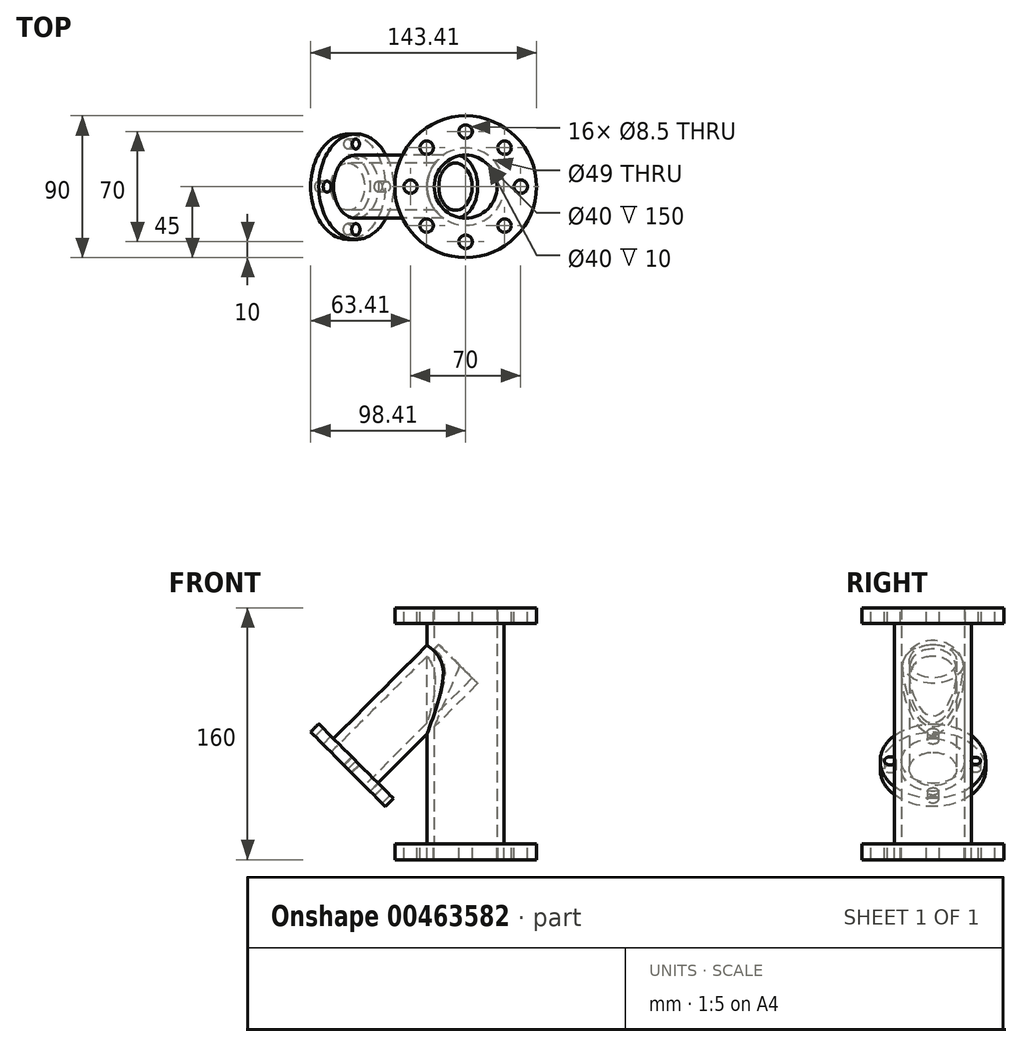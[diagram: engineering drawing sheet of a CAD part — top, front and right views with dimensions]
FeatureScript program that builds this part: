
annotation { "Feature Type Name" : "Feature", "Feature Type Description" : "" }
export const myFeature = defineFeature(function(context is Context, id is Id, definition is map)
    precondition{}
    {
        {
            var Q0;
            Q0=qCreatedBy(makeId("Top.planeOp"),FACE);
            var sketch = newSketch(context, id + "F0", { "sketchPlane" : qUnion([Q0])});
            skCircle(sketch, "E0", {"center": v(0, 0) * mm, "radius": 45 * mm});
            skCircle(sketch, "E1", {"center": v(0, 0) * mm, "radius": 35 * mm, "construction": true});
            skCircle(sketch, "E2", {"center": v(0, 0) * mm, "radius": 24.5 * mm, "construction": true});
            skCircle(sketch, "E3", {"center": v(0, 0) * mm, "radius": 20 * mm});
            skSolve(sketch);
        }
        {
            var Q0;
            Q0=makeQuery(id+"F0.imprint","IMPRINT",FACE,{"disambiguationData":[TD([[makeQuery(id+"F0.imprint","IMPRINT",EDGE,{"derivedFrom":sQuery(id+"F0.wireOp",EDGE,"E0")}),1.0]])]});
            extrude(context, id + "F1", {"entities" : qUnion([Q0]), "depth" : 10 * mm});
        }
        {
            var Q0;
            Q0=makeQuery(id+"F1.opExtrude","CAP_FACE",FACE,{"disambiguationData":[OSD([sQuery(id+"F0.wireOp",EDGE,"E0"),sQuery(id+"F0.wireOp",EDGE,"E3")])],"isStart":true});
            var sketch = newSketch(context, id + "F2", { "sketchPlane" : qUnion([Q0])});
            skCircle(sketch, "E4", {"center": v(0, 0) * mm, "radius": 20 * mm});
            skCircle(sketch, "E5", {"center": v(0, 0) * mm, "radius": 24.5 * mm});
            skSolve(sketch);
        }
        {
            var Q0;
            Q0=makeQuery(id+"F2.imprint","IMPRINT",FACE,{"disambiguationData":[TD([[makeQuery(id+"F2.imprint","IMPRINT",EDGE,{"derivedFrom":sQuery(id+"F2.wireOp",EDGE,"E4")}),1.0]])]});
            extrude(context, id + "F3", {"entities" : qUnion([Q0]), "operationType" : NewBodyOperationType.ADD, "depth" : 140 * mm});
        }
        {
            var Q0;
            Q0=makeQuery(id+"F3.opExtrude","CAP_FACE",FACE,{"disambiguationData":[OSD([sQuery(id+"F2.wireOp",EDGE,"E4"),sQuery(id+"F2.wireOp",EDGE,"E5")])],"isStart":false});
            var sketch = newSketch(context, id + "F4", { "sketchPlane" : qUnion([Q0])});
            skCircle(sketch, "E6", {"center": v(0, 0) * mm, "radius": 45 * mm});
            skSolve(sketch);
        }
        {
            var Q0;
            Q0=makeQuery(id+"F4.imprint","IMPRINT",FACE,{"disambiguationData":[TD([[makeQuery(id+"F4.imprint","IMPRINT",EDGE,{"derivedFrom":sQuery(id+"F4.wireOp",EDGE,"E6")}),1.0]])]});
            extrude(context, id + "F5", {"entities" : qUnion([Q0]), "depth" : 10 * mm});
        }
        {
            var Q0;
            Q0=makeQuery(id+"F1.opExtrude","CAP_FACE",FACE,{"disambiguationData":[OSD([sQuery(id+"F0.wireOp",EDGE,"E0"),sQuery(id+"F0.wireOp",EDGE,"E3")])],"isStart":false});
            var sketch = newSketch(context, id + "F6", { "sketchPlane" : qUnion([Q0])});
            skCircle(sketch, "E7", {"center": v(0, 0) * mm, "radius": 35 * mm});
            skLineSegment(sketch, "E8", {"start": v(0, 0) * mm, "end": v(0, 56.28) * mm});
            skLineSegment(sketch, "E9", {"start": v(0, 0) * mm, "end": v(57.25, 0) * mm});
            skLineSegment(sketch, "E10", {"start": v(0, 0) * mm, "end": v(0, -50.97) * mm});
            skLineSegment(sketch, "E11", {"start": v(0, 0) * mm, "end": v(-60.87, 0) * mm});
            skLineSegment(sketch, "E12", {"start": v(0, 0) * mm, "end": v(-45.46, 45.46) * mm});
            skLineSegment(sketch, "E13", {"start": v(-45.46, 45.46) * mm, "end": v(0, 0) * mm});
            skLineSegment(sketch, "E14", {"start": v(0, 0) * mm, "end": v(45.46, 45.46) * mm});
            skLineSegment(sketch, "E15", {"start": v(0, 0) * mm, "end": v(45.46, -45.46) * mm});
            skLineSegment(sketch, "E16", {"start": v(45.46, -45.46) * mm, "end": v(0, 0) * mm});
            skLineSegment(sketch, "E17", {"start": v(0, 0) * mm, "end": v(-45.46, -45.46) * mm});
            skCircle(sketch, "E18", {"center": v(-24.75, 24.75) * mm, "radius": 4.89 * mm});
            skCircle(sketch, "E19", {"center": v(0, 35) * mm, "radius": 4.1 * mm});
            skCircle(sketch, "E20", {"center": v(24.75, 24.75) * mm, "radius": 6.25 * mm});
            skCircle(sketch, "E21", {"center": v(35, 0) * mm, "radius": 5.32 * mm});
            skCircle(sketch, "E22", {"center": v(24.75, -24.75) * mm, "radius": 3.02 * mm});
            skCircle(sketch, "E23", {"center": v(0, -35) * mm, "radius": 3.8 * mm});
            skCircle(sketch, "E24", {"center": v(-24.75, -24.75) * mm, "radius": 6.14 * mm});
            skCircle(sketch, "E25", {"center": v(-35, 0) * mm, "radius": 5.66 * mm});
            skSolve(sketch);
        }
        {
            var Q0;
            Q0=sQuery(id+"F6.wireOp",VERTEX,"E18.center");
            var Q1;
            Q1=sQuery(id+"F6.wireOp",VERTEX,"E19.center");
            var Q2;
            Q2=sQuery(id+"F6.wireOp",VERTEX,"E20.center");
            var Q3;
            Q3=sQuery(id+"F6.wireOp",VERTEX,"E21.center");
            var Q4;
            Q4=sQuery(id+"F6.wireOp",VERTEX,"E22.center");
            var Q5;
            Q5=sQuery(id+"F6.wireOp",VERTEX,"E23.center");
            var Q6;
            Q6=sQuery(id+"F6.wireOp",VERTEX,"E24.center");
            var Q7;
            Q7=sQuery(id+"F6.wireOp",VERTEX,"E25.center");
            var Q8;
            Q8=makeQuery(id+"F1.opExtrude","SWEPT_BODY",BODY,{"disambiguationData":[OSD([sQuery(id+"F0.wireOp",EDGE,"E0"),sQuery(id+"F0.wireOp",EDGE,"E3")])]});
            var Q9;
            Q9=makeQuery(id+"F5.opExtrude","SWEPT_BODY",BODY,{"disambiguationData":[OSD([sQuery(id+"F2.wireOp",EDGE,"E5"),sQuery(id+"F4.wireOp",EDGE,"E6")])]});
            hole(context, id + "F7", {"style" : HoleStyle.SIMPLE, "endStyle" : HoleEndStyle.THROUGH, "holeDiameter" : 8.5 * mm, "isTappedThrough" : true, "tappedDepth" : 12 * mm, "tapClearance" : 3, "locations" : qUnion([Q0, Q1, Q2, Q3, Q4, Q5, Q6, Q7]), "scope" : qUnion([Q8, Q9])});
        }
        {
            var Q0;
            Q0=makeQuery(id+"F3.opExtrude","CAP_FACE",FACE,{"disambiguationData":[OSD([sQuery(id+"F2.wireOp",EDGE,"E4"),sQuery(id+"F2.wireOp",EDGE,"E5")])],"isStart":false});
            var sketch = newSketch(context, id + "F8", { "sketchPlane" : qUnion([Q0])});
            skCircle(sketch, "E26", {"center": v(0, 0) * mm, "radius": 24.5 * mm});
            skCircle(sketch, "E27", {"center": v(0, 0) * mm, "radius": 20 * mm});
            skSolve(sketch);
        }
        {
            var Q0;
            Q0=makeQuery(id+"F8.imprint","IMPRINT",FACE,{"disambiguationData":[TD([[makeQuery(id+"F8.imprint","IMPRINT",EDGE,{"derivedFrom":sQuery(id+"F8.wireOp",EDGE,"E26")}),1.0]])]});
            extrude(context, id + "F9", {"entities" : qUnion([Q0]), "depth" : 10 * mm});
        }
        {
            var Q0;
            Q0=qCreatedBy(makeId("Front.planeOp"),FACE);
            var sketch = newSketch(context, id + "F10", { "sketchPlane" : qUnion([Q0])});
            skLineSegment(sketch, "E28", {"start": v(0, 0) * mm, "end": v(0, -87.13) * mm});
            skLineSegment(sketch, "E29", {"start": v(0, 0) * mm, "end": v(0, -40) * mm});
            skLineSegment(sketch, "E30", {"start": v(0, -40) * mm, "end": v(-63.64, -103.64) * mm});
            skLineSegment(sketch, "E31", {"start": v(-63.64, -103.64) * mm, "end": v(-79.75, -87.53) * mm});
            skSolve(sketch);
        }
        {
            var Q0;
            Q0=qCreatedBy(makeId("Right.planeOp"),FACE);
            var Q1;
            Q1=sQuery(id+"F10.wireOp",EDGE,"E31");
            cPlane(context, id + "F11", {"entities" : qUnion([Q0, Q1]), "cplaneType" : CPlaneType.LINE_ANGLE, "offset" : 25 * mm, "angle" : 0 * degree, "width" : 150 * mm, "height" : 150 * mm});
        }
        {
            var Q0;
            Q0=qCreatedBy(id+"F11.planeOp",FACE);
            var sketch = newSketch(context, id + "F12", { "sketchPlane" : qUnion([Q0])});
            skCircle(sketch, "E32", {"center": v(0, -12.36) * mm, "radius": 15 * mm});
            skCircle(sketch, "E33", {"center": v(0, -12.36) * mm, "radius": 20 * mm});
            skSolve(sketch);
        }
        {
            var Q0;
            Q0=makeQuery(id+"F12.imprint","IMPRINT",FACE,{"disambiguationData":[TD([[makeQuery(id+"F12.imprint","IMPRINT",EDGE,{"derivedFrom":sQuery(id+"F12.wireOp",EDGE,"E32")}),-1.0]])]});
            extrude(context, id + "F13", {"entities" : qUnion([Q0]), "operationType" : NewBodyOperationType.ADD, "oppositeDirection" : true, "depth" : 96.8 * mm});
        }
        {
            var Q0;
            Q0=makeQuery(id+"F12.imprint","IMPRINT",FACE,{"disambiguationData":[TD([[makeQuery(id+"F12.imprint","IMPRINT",EDGE,{"derivedFrom":sQuery(id+"F12.wireOp",EDGE,"E32")}),-1.0]])]});
            var sketch = newSketch(context, id + "F14", { "sketchPlane" : qUnion([Q0])});
            skCircle(sketch, "E34", {"center": v(0, -12.61) * mm, "radius": 20 * mm});
            skCircle(sketch, "E35", {"center": v(0, -12.61) * mm, "radius": 33.5 * mm});
            skSolve(sketch);
        }
        {
            var Q0;
            Q0=makeQuery(id+"F14.imprint","IMPRINT",FACE,{"disambiguationData":[TD([[makeQuery(id+"F14.imprint","IMPRINT",EDGE,{"derivedFrom":sQuery(id+"F14.wireOp",EDGE,"E35")}),1.0]])]});
            extrude(context, id + "F15", {"entities" : qUnion([Q0]), "operationType" : NewBodyOperationType.ADD, "oppositeDirection" : true, "depth" : 7.3 * mm});
        }
        {
            var Q0;
            {var subQ0=sQuery(id+"F12.wireOp",EDGE,"E33");Q0=makeQuery(id+"F15.boolean.opBoolean","MERGE",FACE,{"derivedFrom":[makeQuery(id+"F13.opExtrude","CAP_FACE",FACE,{"disambiguationData":[OSD([sQuery(id+"F12.wireOp",EDGE,"E32"),subQ0])],"isStart":true}),makeQuery(id+"F15.opExtrude","CAP_FACE",FACE,{"disambiguationData":[OSD([subQ0,sQuery(id+"F14.wireOp",EDGE,"E34"),sQuery(id+"F14.wireOp",EDGE,"E35")])],"isStart":true})]});}
            var sketch = newSketch(context, id + "F16", { "sketchPlane" : qUnion([Q0])});
            skPoint(sketch, "E36.endSnap0", {"position": v(0, -32.36) * mm});
            skCircle(sketch, "E37", {"center": v(0, 13.4) * mm, "radius": 3.53 * mm});
            skCircle(sketch, "E38", {"center": v(-27.1, -12.36) * mm, "radius": 3.2 * mm});
            skCircle(sketch, "E39", {"center": v(0, -39.8) * mm, "radius": 3.39 * mm});
            skCircle(sketch, "E40", {"center": v(27.17, -12.36) * mm, "radius": 3.66 * mm});
            skPoint(sketch, "E41.trimOffspring.end.orphan", {"position": v(0, -46.12) * mm});
            skPoint(sketch, "E42.orphan", {"position": v(0, -12.36) * mm});
            skSolve(sketch);
        }
        {
            var Q0;
            Q0=makeQuery(id+"F16.imprint","IMPRINT",FACE,{"disambiguationData":[TD([[makeQuery(id+"F16.imprint","IMPRINT",EDGE,{"derivedFrom":sQuery(id+"F16.wireOp",EDGE,"E40")}),1.0]])]});
            var Q1;
            Q1=makeQuery(id+"F16.imprint","IMPRINT",FACE,{"disambiguationData":[TD([[makeQuery(id+"F16.imprint","IMPRINT",EDGE,{"derivedFrom":sQuery(id+"F16.wireOp",EDGE,"E37")}),1.0]])]});
            var Q2;
            Q2=makeQuery(id+"F16.imprint","IMPRINT",FACE,{"disambiguationData":[TD([[makeQuery(id+"F16.imprint","IMPRINT",EDGE,{"derivedFrom":sQuery(id+"F16.wireOp",EDGE,"E38")}),1.0]])]});
            var Q3;
            Q3=makeQuery(id+"F16.imprint","IMPRINT",FACE,{"disambiguationData":[TD([[makeQuery(id+"F16.imprint","IMPRINT",EDGE,{"derivedFrom":sQuery(id+"F16.wireOp",EDGE,"E39")}),1.0]])]});
            extrude(context, id + "F17", {"entities" : qUnion([Q0, Q1, Q2, Q3]), "operationType" : NewBodyOperationType.REMOVE, "oppositeDirection" : true, "depth" : 25 * mm});
        }
    });
